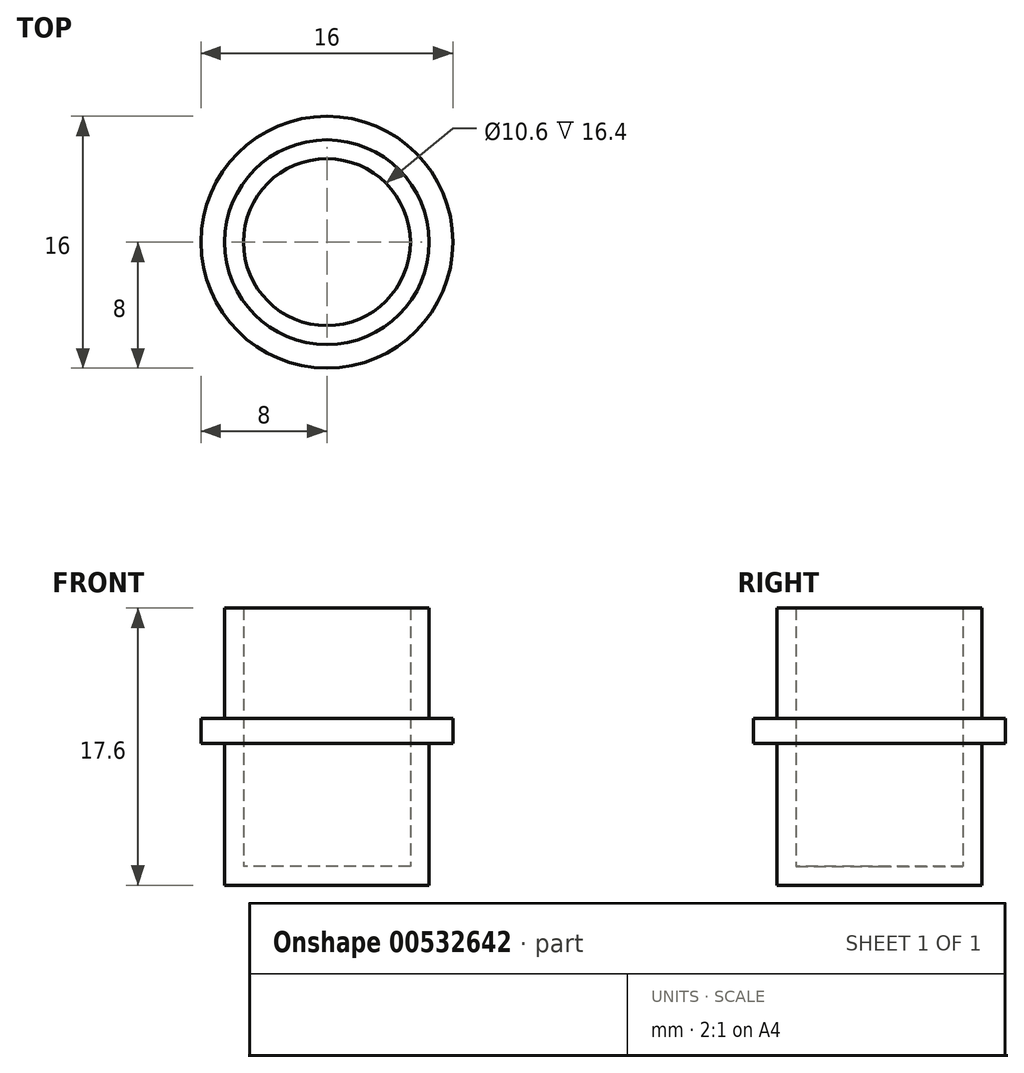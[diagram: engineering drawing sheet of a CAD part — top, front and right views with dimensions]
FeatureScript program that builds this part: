
annotation { "Feature Type Name" : "Feature", "Feature Type Description" : "" }
export const myFeature = defineFeature(function(context is Context, id is Id, definition is map)
    precondition{}
    {
        {
            var Q0;
            Q0=qCreatedBy(makeId("Top.planeOp"),FACE);
            var sketch = newSketch(context, id + "F0", { "sketchPlane" : qUnion([Q0])});
            skCircle(sketch, "E0", {"center": v(0, 0) * mm, "radius": 6.5 * mm});
            skSolve(sketch);
        }
        {
            var Q0;
            Q0 = qSketchRegion(id + "F0", true);
            extrude(context, id + "F1", {"entities" : qUnion([Q0]), "depth" : 9 * mm, "offsetDistance" : 25 * mm});
        }
        {
            var Q0;
            Q0=makeQuery(id+"F1.opExtrude","CAP_FACE",FACE,{"disambiguationData":[OSD([sQuery(id+"F0.wireOp",EDGE,"E0")])],"isStart":false});
            var sketch = newSketch(context, id + "F2", { "sketchPlane" : qUnion([Q0])});
            skCircle(sketch, "E1", {"center": v(0, 0) * mm, "radius": 8 * mm});
            skSolve(sketch);
        }
        {
            var Q0;
            Q0 = qSketchRegion(id + "F2", true);
            extrude(context, id + "F3", {"entities" : qUnion([Q0]), "operationType" : NewBodyOperationType.ADD, "depth" : 1.6 * mm, "offsetDistance" : 25 * mm});
        }
        {
            var Q0;
            Q0=makeQuery(id+"F3.opExtrude","CAP_FACE",FACE,{"disambiguationData":[OSD([sQuery(id+"F2.wireOp",EDGE,"E1")])],"isStart":false});
            var sketch = newSketch(context, id + "F4", { "sketchPlane" : qUnion([Q0])});
            skCircle(sketch, "E2", {"center": v(0, 0) * mm, "radius": 6.5 * mm});
            skSolve(sketch);
        }
        {
            var Q0;
            Q0 = qSketchRegion(id + "F4", true);
            extrude(context, id + "F5", {"entities" : qUnion([Q0]), "operationType" : NewBodyOperationType.ADD, "depth" : 7 * mm, "offsetDistance" : 25 * mm});
        }
        {
            var Q0;
            Q0=makeQuery(id+"F5.opExtrude","CAP_FACE",FACE,{"disambiguationData":[OSD([sQuery(id+"F4.wireOp",EDGE,"E2")])],"isStart":false});
            shell(context, id + "F6", {"entities" : qUnion([Q0]), "thickness" : 1.2 * mm});
        }
    });
